# Revit family: Type 75_Mini_Wall Light E27
name_source: partatom
category: Lighting Fixtures
revit_build: Autodesk Revit 2016 (Build: 20150220_1215(x64)
units: mm (PartAtom-declared; Revit-internal decimal feet)

## family parameters
Always vertical = Yes
Cut with Voids When Loaded = No
Light Source = No
OmniClass Number = 23.80.70.11.14
OmniClass Title = General Luminaries, Directional
Part Type = Normal
Room Calculation Point = No
Round Connector Dimension = Use Diameter
Shared = No
Work Plane-Based = No

## types (1)
- Type 75 Mini Wall Light
    Brand URL = www.anglepoise.com
    Edition number = Type75
    Energy Efficiency Class = Compatible with lamps from A+ to E
    IP Rating = IP20
    Lamp = E27 Lamp UK/EU
    Manufacturer Name = Anglepoise
    Manufacturer country = China
    Material = Aluminium & Steel - Painted / Plated /Anodised
    Material Main = Aluminium
    Material Secondary = Steel
    Mounting = Wall Mounted
    Product family = Wall Light
    Wattage Comments = Max 20W CFL  Max 10W LED
    Weight = 0.35Kg

## geometry (parser evidence)
native form markers: Sweep x3
no freeform markers — native parametric forms only
